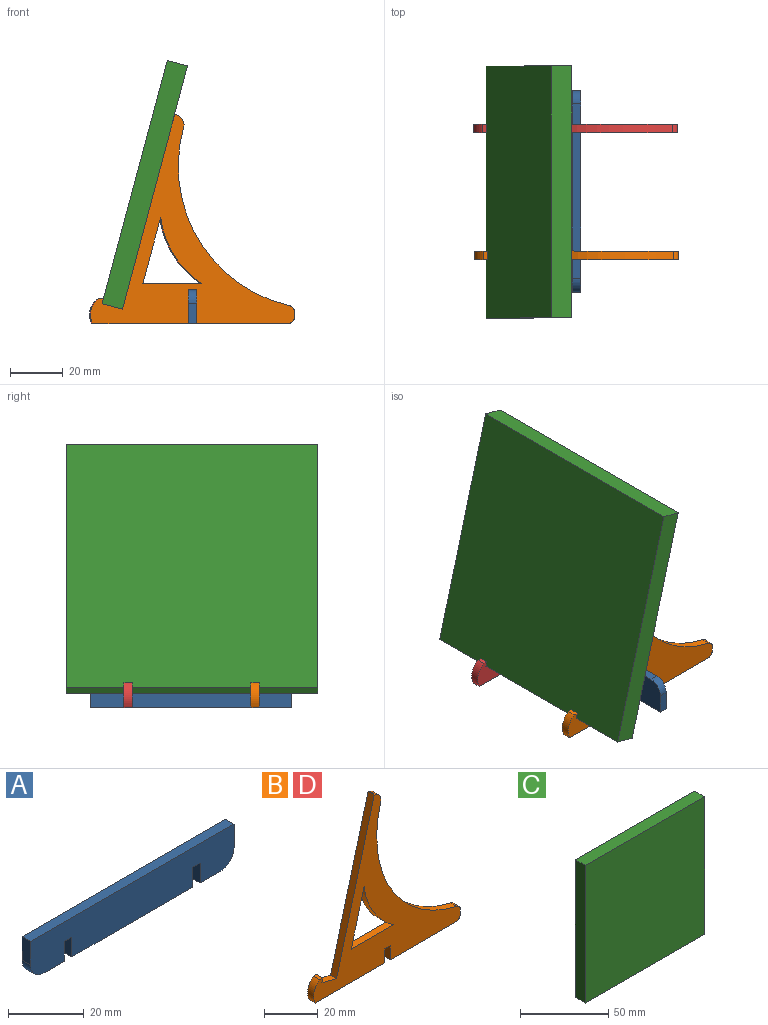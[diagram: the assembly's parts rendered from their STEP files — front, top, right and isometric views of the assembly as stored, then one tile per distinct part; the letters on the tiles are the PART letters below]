
ASSEMBLY  parts=4 mates=9
PART A: 16 faces, bbox 76.2x3.2x12.7 mm
  f0: plane 45.21x3.18mm, normal (0,0,-1), area 143.5mm2, adj f6,f7,f9,f13
  f1: plane 7.62x3.18mm, normal (0,0,-1), area 24.2mm2, adj f6,f7,f10,f15
  f2: plane 76.2x3.18mm, normal (0,0,1), area 241.9mm2, adj f3,f5,f6,f7
  f3: plane 7.62x3.18mm, normal (-1,0,0), area 24.2mm2, adj f2,f6,f7,f14
  f4: plane 7.62x3.18mm, normal (0,0,-1), area 24.2mm2, adj f6,f7,f12,f14
  f5: plane 7.62x3.18mm, normal (1,0,0), area 24.2mm2, adj f2,f6,f7,f15
  f6: plane 76.2x12.7mm, normal (0,-1,0), area 921.2mm2, adj f0,f1,f2,f3,f4,f5,f8,f9
  f7: plane 76.2x12.7mm, normal (0,1,0), area 921.2mm2, adj f0,f1,f2,f3,f4,f5,f8,f9
  f8: plane 3.18x2.79mm, normal (0,0,-1), area 8.9mm2, adj f6,f7,f9,f10
  f9: plane 6.35x3.18mm, normal (1,0,0), area 20.2mm2, adj f0,f6,f7,f8
  f10: plane 6.35x3.18mm, normal (-1,0,0), area 20.2mm2, adj f1,f6,f7,f8
  f11: plane 3.18x2.79mm, normal (0,0,-1), area 8.9mm2, adj f6,f7,f12,f13
  f12: plane 6.35x3.18mm, normal (1,0,0), area 20.2mm2, adj f4,f6,f7,f11
  f13: plane 6.35x3.18mm, normal (-1,0,0), area 20.2mm2, adj f0,f6,f7,f11
  f14: cylinder r=5.08mm len=5.08mm, axis (0,1,0), area 25.3mm2, adj f3,f4,f6,f7
  f15: cylinder r=5.08mm len=5.08mm, axis (0,-1,0), area 25.3mm2, adj f1,f5,f6,f7
PART B: 21 faces, bbox 77.1x3.2x79.1 mm
  f0: plane 79.09x77.12mm, normal (0,-1,0), area 1670.3mm2, adj f2,f3,f4,f5,f6,f7,f8,f9
  f1: plane 79.09x77.12mm, normal (0,1,0), area 1670.3mm2, adj f2,f3,f4,f5,f6,f7,f8,f9
  f2: plane 6.35x3.18mm, normal (1,0,0), area 20.2mm2, adj f0,f1,f3,f14
  f3: plane 3.18x2.79mm, normal (0,0,-1), area 8.9mm2, adj f0,f1,f2,f4
  f4: plane 6.35x3.18mm, normal (-1,0,0), area 20.2mm2, adj f0,f1,f3,f5
  f5: plane 34.43x3.18mm, normal (0,0,-1), area 109.3mm2, adj f0,f1,f4,f15
  f6: plane 3.18x1.75mm, normal (1,0,0), area 5.5mm2, adj f0,f1,f15,f16
  f7: cylinder r=54mm len=67.41mm, axis (0,1,0), area 278.3mm2, adj f0,f1,f16,f17
  f8: plane 3.18x0.73mm, normal (0.26,0,0.97), area 2.4mm2, adj f0,f1,f9,f17
  f9: plane 73.6x19.72mm, normal (-0.97,0,0.26), area 241.9mm2, adj f0,f1,f8,f10
  f10: plane 7.67x3.18mm, normal (0.26,0,0.97), area 25.2mm2, adj f0,f1,f9,f11
  f11: plane 3.18x1.88mm, normal (0.97,0,-0.26), area 6.2mm2, adj f0,f1,f10,f12
  f12: plane 3.18x1.59mm, normal (0,0,1), area 5mm2, adj f0,f1,f11,f13
  f13: cylinder r=6.99mm len=9.42mm, axis (0,1,0), area 34.1mm2, adj f0,f1,f12,f14
  f14: plane 36.44x3.18mm, normal (0,0,-1), area 115.7mm2, adj f0,f1,f2,f13
  f15: cylinder r=2.54mm len=3.18mm, axis (0,-1,0), area 12.7mm2, adj f0,f1,f5,f6
  f16: cylinder r=2.54mm len=3.18mm, axis (0,1,0), area 10.9mm2, adj f0,f1,f6,f7
  f17: cylinder r=3.81mm len=4.72mm, axis (0,1,0), area 19.2mm2, adj f0,f1,f7,f8
  f18: plane 24.93x6.73mm, normal (0.97,0,-0.26), area 82mm2, adj f0,f1,f19,f20
  f19: plane 22.19x3.18mm, normal (0,0,1), area 70.5mm2, adj f0,f1,f18,f20
  f20: cylinder r=35.41mm len=24.93mm, axis (0,-1,0), area 96mm2, adj f0,f1,f18,f19
PART C: 6 faces, bbox 95.3x7.9x95.3 mm
  f0: plane 95.25x7.94mm, normal (0,0,1), area 756mm2, adj f1,f3,f4,f5
  f1: plane 95.25x7.94mm, normal (-1,0,0), area 756mm2, adj f0,f2,f4,f5
  f2: plane 95.25x7.94mm, normal (0,0,-1), area 756mm2, adj f1,f3,f4,f5
  f3: plane 95.25x7.94mm, normal (1,0,0), area 756mm2, adj f0,f2,f4,f5
  f4: plane 95.25x95.25mm, normal (0,-1,0), area 9072.6mm2, adj f0,f1,f2,f3
  f5: plane 95.25x95.25mm, normal (0,1,0), area 9072.6mm2, adj f0,f1,f2,f3
PART D: same geometry as B
PLACE A rot(axis=(-0.71,0.71,0),180deg) t=(90.66,-44.04,-1.12)mm
PLACE B t=(109.81,-104.75,-1.12)mm
PLACE C rot(axis=(-0.13,0.13,-0.98),91deg) t=(77.53,-81.76,48.28)mm
PLACE D t=(109.43,-56.74,-1.12)mm
MATE planar C.f2 <-> D.f10  axis (-0.26,0,-0.97) through (61.91,-82.46,5.29)mm
MATE planar A.f9 <-> B.f1  axis (0,-1,0) through (92.25,-104.75,8.4)mm
MATE planar C.f5 <-> B.f9  axis (0.97,0,-0.26) through (78.07,-82.46,50.27)mm
MATE planar A.f2 <-> B.f5  axis (0,0,-1) through (92.25,-82.14,-1.12)mm
MATE planar D.f1 <-> A.f12  axis (0,1,0) through (88.92,-56.74,19.6)mm
MATE planar A.f2 <-> D.f5  axis (0,0,-1) through (92.25,-82.14,-1.12)mm
MATE planar A.f6 <-> B.f4  axis (1,0,0) through (93.84,-111.35,11.58)mm
MATE parallel C.f5 <-> D.f9  axis (0.97,0,-0.26) through (78.07,-82.46,50.27)mm
MATE planar D.f2 <-> A.f7  axis (1,0,0) through (90.66,-58.33,2.05)mm
